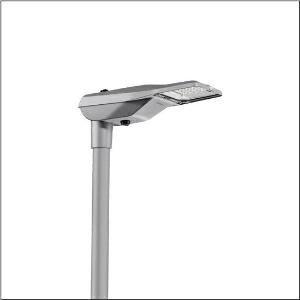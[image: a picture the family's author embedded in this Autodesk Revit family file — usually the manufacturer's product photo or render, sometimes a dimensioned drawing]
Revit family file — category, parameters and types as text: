
# Revit family: streetlight_sl_21_iq_micro___pl52_5xe1h31y08db_0e41
name_source: partatom
category: Lighting Fixtures
units: mm (PartAtom-declared; Revit-internal decimal feet)

## family parameters
Cut with Voids When Loaded = No
Host = Face
Light Source = No
Part Type = Normal
Room Calculation Point = No
Round Connector Dimension = Use Diameter
Shared = No

## types (1)
- --- (1 x LED, 5030 lm, 39.1 W, 3000K)
    Apparent Load = 39 VA
    CIE Flux Codes = 27 59 98 100 100
    Color Rendering = 70
    Color Temperature = 3000K
    Default Elevation = 1800 mm
    Description = Streetlight SL 21 iQ micro, mast luminaire, primary light control with lens, of PMMA, primary optical cover: cover, of toughened safety glass, transparent, light distribution: PL52, light emission: direct distribution, primary light characteristic: asymmetric, installation type: post-top, side-entry, LED, High Power LED, rated luminous flux: 5.030lm, luminous efficacy: 129lm/W, light colour: 730, colour temperature: 3000K, control: pre-setting: logarithmic dimming characteristic, Street-Remote, Auto-Match, Temp-Guard, Lumen-Switch, Night-Set, Smart-Wire, Light-Fading, Desk-Remote (wireless, voltage-free reading and setting of iQ features in the workshop via application-optimized NFC function/RFID function), optimised constant luminous flux control (CLO 2.0), mains connection: 220..240V, AC, 50/60Hz, start of lifetime: 39W, end of service life: 41W, reduction: 17W, luminaire housing, of diecast aluminium, powder-coated, Siteco® metallic grey (DB 702S), corrosivity category C5 mid according to DIN EN ISO 12944, please order mast flange separately, inclination adjustable: 0°, 5°, 10°, 15°, sealing non-destructively replaceable, multi-level sealing system, length: 528mm, width: 235mm, height: 110mm, mast flange for spigot size: 42mm (side-entry): 5XC10008XM4, 60/48mm (side-entry/post-top): 5XC10108XM2, 76/60mm (side-entry/post-top): 5XC10108XM1, Smart Interface below and above, protection rating (complete): IP66, insulation class (complete): insulation class II (safety insulation), certification: CE, ENEC, ENEC+, VDE, impact resistance: IK09, permissible operating ambient temperature for outdoor applications: -40..+50°C, standard-compliant lighting for roads and squares, packaging unit: 1 piece

Light Distribution: PL52
    Height = 110 mm
    Lamp = 1 x LED
    Lamp Light Flux = 5030 lm
    Lamp Power = 39.1 W
    Lamp count = 1
    Length = 528 mm
    Luminous efficacy = 129 lm/W
    Manufacturer = Siteco
    ModVariant = No
    Model = 5XE1H31Y08DB
    Number of Poles = 1
    OnlyDefault = Yes
    Power Factor = 1
    Product Name = Streetlight SL 21 iQ micro | PL52
    Product group = mast luminaire | pylon top
    ProductGroupID = 6100
    Protection Class = Protection class II
    Protection Degree = IP 66
    RLX_Detail_Level = 1
    RLX_Emergency_Light_Flux = 0 lm
    RLX_Emergency_Type = 0
    RLX_Emergency_Type_DB = No
    RlxData = <blob elided: 108065 chars, md5=8baae8c0>
    Socket = socket
    Standby Power = 0 W
    System Light Flux = 5030 lm
    System Power = 39 W
    Type Comments = factory setting: luminous flux: 100 % | dim-lin: 254 | 765 mA
    Type Image = l_1007239.jpg
    URL = http://relux.com
    VarID = @adj_084837
    Voltage = 0 V
    Weight = 0.00 kg
    Width = 235 mm

## geometry (parser evidence)
native form markers: Blend x4, Sweep x8
no freeform markers — native parametric forms only
